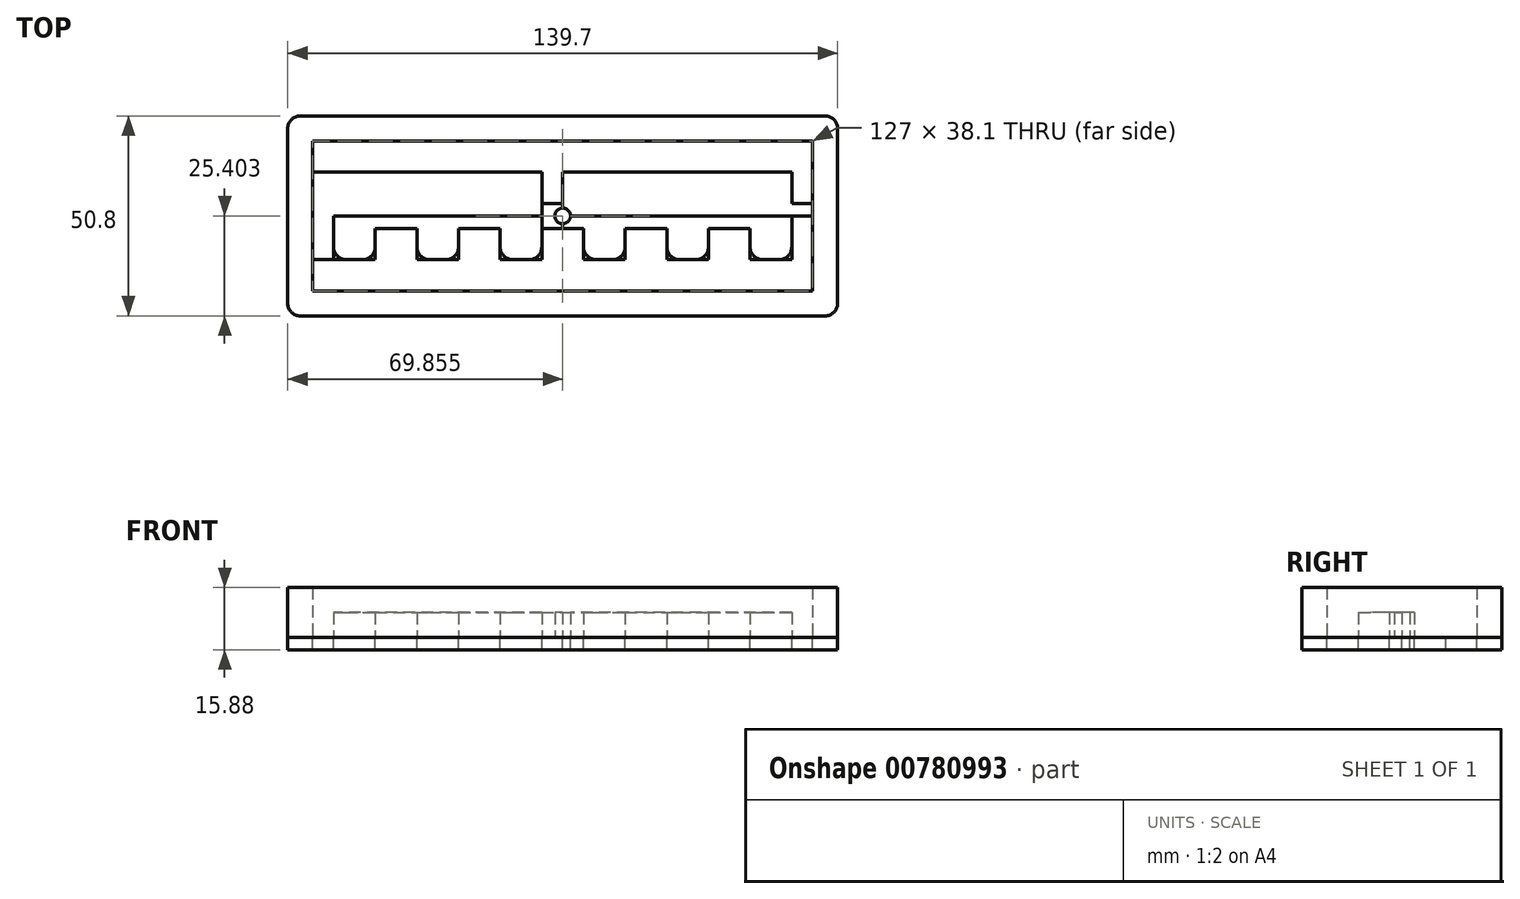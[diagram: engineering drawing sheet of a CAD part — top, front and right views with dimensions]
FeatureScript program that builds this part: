
annotation { "Feature Type Name" : "Feature", "Feature Type Description" : "" }
export const myFeature = defineFeature(function(context is Context, id is Id, definition is map)
    precondition{}
    {
        {
            var Q0;
            Q0=qCreatedBy(makeId("Top.planeOp"),FACE);
            var sketch = newSketch(context, id + "F0", { "sketchPlane" : qUnion([Q0])});
            skLineSegment(sketch, "E0.bottom", {"start": v(-62.65, 20.21) * mm, "end": v(77.05, 20.21) * mm});
            skLineSegment(sketch, "E0.top", {"start": v(-62.65, -30.59) * mm, "end": v(77.05, -30.59) * mm});
            skLineSegment(sketch, "E0.left", {"start": v(-62.65, 20.21) * mm, "end": v(-62.65, -30.59) * mm});
            skLineSegment(sketch, "E0.right", {"start": v(77.05, 20.21) * mm, "end": v(77.05, -30.59) * mm});
            skLineSegment(sketch, "E1.bottom", {"start": v(-56.3, 13.86) * mm, "end": v(70.7, 13.86) * mm});
            skLineSegment(sketch, "E1.top", {"start": v(-56.3, -24.24) * mm, "end": v(70.7, -24.24) * mm});
            skLineSegment(sketch, "E1.left", {"start": v(-56.3, 13.86) * mm, "end": v(-56.3, -24.24) * mm});
            skLineSegment(sketch, "E1.right", {"start": v(70.7, 13.86) * mm, "end": v(70.7, -24.24) * mm});
            skLineSegment(sketch, "E2", {"start": v(-56.3, 13.86) * mm, "end": v(-56.3, 20.21) * mm});
            skLineSegment(sketch, "E3", {"start": v(-56.3, 13.86) * mm, "end": v(-62.65, 13.86) * mm});
            skLineSegment(sketch, "E4", {"start": v(70.7, 13.86) * mm, "end": v(70.7, -5.19) * mm});
            skLineSegment(sketch, "E5", {"start": v(70.7, -5.19) * mm, "end": v(-56.3, -5.19) * mm});
            skLineSegment(sketch, "E6", {"start": v(-56.3, -5.19) * mm, "end": v(-56.3, -2.01) * mm});
            skLineSegment(sketch, "E7", {"start": v(-56.3, -5.19) * mm, "end": v(-56.3, -8.36) * mm});
            skLineSegment(sketch, "E8", {"start": v(-56.3, -8.36) * mm, "end": v(70.7, -8.36) * mm});
            skLineSegment(sketch, "E9", {"start": v(-56.3, -2.01) * mm, "end": v(70.7, -2.01) * mm});
            skLineSegment(sketch, "E10", {"start": v(-56.3, 13.86) * mm, "end": v(7.2, 13.86) * mm});
            skLineSegment(sketch, "E11", {"start": v(-56.3, -2.01) * mm, "end": v(-35.13, -2.01) * mm});
            skLineSegment(sketch, "E12", {"start": v(7.2, 13.86) * mm, "end": v(7.2, -2.01) * mm});
            skLineSegment(sketch, "E13", {"start": v(-35.13, -2.01) * mm, "end": v(-13.96, -2.01) * mm});
            skLineSegment(sketch, "E14", {"start": v(7.2, -2.01) * mm, "end": v(28.37, -2.01) * mm});
            skLineSegment(sketch, "E15", {"start": v(28.37, -2.01) * mm, "end": v(49.54, -2.01) * mm});
            skLineSegment(sketch, "E16", {"start": v(-35.13, -2.01) * mm, "end": v(-45.71, -2.01) * mm});
            skLineSegment(sketch, "E17", {"start": v(-35.13, -2.01) * mm, "end": v(-24.55, -2.01) * mm});
            skLineSegment(sketch, "E18", {"start": v(-13.96, -2.01) * mm, "end": v(-3.38, -2.01) * mm});
            skLineSegment(sketch, "E19", {"start": v(7.2, -2.01) * mm, "end": v(17.79, -2.01) * mm});
            skLineSegment(sketch, "E20", {"start": v(49.54, -2.01) * mm, "end": v(60.12, -2.01) * mm});
            skLineSegment(sketch, "E21", {"start": v(28.37, -2.01) * mm, "end": v(38.95, -2.01) * mm});
            skLineSegment(sketch, "E22", {"start": v(-35.13, -2.01) * mm, "end": v(-40.42, -2.01) * mm});
            skLineSegment(sketch, "E23", {"start": v(-56.3, -2.01) * mm, "end": v(-51, -2.01) * mm});
            skLineSegment(sketch, "E24", {"start": v(-51, -2.01) * mm, "end": v(-51, -8.36) * mm});
            skLineSegment(sketch, "E25", {"start": v(-40.42, -2.01) * mm, "end": v(-40.42, -8.36) * mm});
            skLineSegment(sketch, "E26", {"start": v(-35.13, -2.01) * mm, "end": v(-29.84, -2.01) * mm});
            skLineSegment(sketch, "E27", {"start": v(-13.96, -2.01) * mm, "end": v(-19.25, -2.01) * mm});
            skLineSegment(sketch, "E28", {"start": v(-29.84, -2.01) * mm, "end": v(-29.84, -8.36) * mm});
            skLineSegment(sketch, "E29", {"start": v(-19.25, -2.01) * mm, "end": v(-19.25, -8.36) * mm});
            skLineSegment(sketch, "E30", {"start": v(-13.96, -2.01) * mm, "end": v(-8.67, -2.01) * mm});
            skLineSegment(sketch, "E31", {"start": v(-8.67, -2.01) * mm, "end": v(-8.67, -8.36) * mm});
            skLineSegment(sketch, "E32", {"start": v(-3.38, -2.01) * mm, "end": v(1.91, -2.01) * mm});
            skLineSegment(sketch, "E33", {"start": v(1.91, -2.01) * mm, "end": v(1.91, -8.36) * mm});
            skLineSegment(sketch, "E34", {"start": v(7.2, -2.01) * mm, "end": v(12.5, -2.01) * mm});
            skLineSegment(sketch, "E35", {"start": v(12.5, -2.01) * mm, "end": v(12.5, -8.36) * mm});
            skLineSegment(sketch, "E36", {"start": v(17.79, -2.01) * mm, "end": v(23.08, -2.01) * mm});
            skLineSegment(sketch, "E37", {"start": v(23.08, -2.01) * mm, "end": v(23.08, -8.36) * mm});
            skLineSegment(sketch, "E38", {"start": v(28.37, -2.01) * mm, "end": v(33.66, -2.01) * mm});
            skLineSegment(sketch, "E39", {"start": v(33.66, -2.01) * mm, "end": v(33.66, -8.36) * mm});
            skLineSegment(sketch, "E40", {"start": v(38.95, -2.01) * mm, "end": v(44.25, -2.01) * mm});
            skLineSegment(sketch, "E41", {"start": v(44.25, -2.01) * mm, "end": v(44.25, -8.36) * mm});
            skLineSegment(sketch, "E42", {"start": v(49.54, -2.01) * mm, "end": v(54.83, -2.01) * mm});
            skLineSegment(sketch, "E43", {"start": v(54.83, -2.01) * mm, "end": v(54.83, -8.36) * mm});
            skLineSegment(sketch, "E44", {"start": v(60.12, -2.01) * mm, "end": v(65.41, -2.01) * mm});
            skLineSegment(sketch, "E45", {"start": v(65.41, -2.01) * mm, "end": v(65.41, -8.36) * mm});
            skLineSegment(sketch, "E46", {"start": v(-56.3, -2.01) * mm, "end": v(-56.3, 5.93) * mm});
            skLineSegment(sketch, "E47", {"start": v(-56.3, 5.93) * mm, "end": v(70.7, 5.93) * mm});
            skLineSegment(sketch, "E48", {"start": v(-51, -2.01) * mm, "end": v(-51, 5.93) * mm});
            skLineSegment(sketch, "E49", {"start": v(-40.42, -2.01) * mm, "end": v(-40.42, 5.93) * mm});
            skLineSegment(sketch, "E50", {"start": v(-29.84, -2.01) * mm, "end": v(-29.84, 5.93) * mm});
            skLineSegment(sketch, "E51", {"start": v(-19.25, -2.01) * mm, "end": v(-19.25, 5.93) * mm});
            skLineSegment(sketch, "E52", {"start": v(-8.67, -2.01) * mm, "end": v(-8.67, 5.93) * mm});
            skLineSegment(sketch, "E53", {"start": v(1.91, -2.01) * mm, "end": v(1.91, 5.93) * mm});
            skPoint(sketch, "E53.endSnap0", {"position": v(7.2, 5.93) * mm});
            skLineSegment(sketch, "E54", {"start": v(12.5, -2.01) * mm, "end": v(12.5, 5.93) * mm});
            skLineSegment(sketch, "E55", {"start": v(23.08, 5.93) * mm, "end": v(23.08, -2.01) * mm});
            skLineSegment(sketch, "E56", {"start": v(33.66, -2.01) * mm, "end": v(33.66, 5.93) * mm});
            skLineSegment(sketch, "E57", {"start": v(44.25, -2.01) * mm, "end": v(44.25, 5.93) * mm});
            skLineSegment(sketch, "E58", {"start": v(54.83, -2.01) * mm, "end": v(54.83, 5.93) * mm});
            skLineSegment(sketch, "E59", {"start": v(65.41, -2.01) * mm, "end": v(65.41, 5.93) * mm});
            skLineSegment(sketch, "E60", {"start": v(-56.3, -8.36) * mm, "end": v(-56.3, -16.3) * mm});
            skLineSegment(sketch, "E61", {"start": v(-56.3, -16.3) * mm, "end": v(70.7, -16.3) * mm});
            skLineSegment(sketch, "E62", {"start": v(-51, -8.36) * mm, "end": v(-51, -16.3) * mm});
            skLineSegment(sketch, "E63", {"start": v(-40.42, -8.36) * mm, "end": v(-40.42, -16.3) * mm});
            skLineSegment(sketch, "E64", {"start": v(-29.84, -8.36) * mm, "end": v(-29.84, -16.3) * mm});
            skLineSegment(sketch, "E65", {"start": v(-19.25, -8.36) * mm, "end": v(-19.25, -16.3) * mm});
            skLineSegment(sketch, "E66", {"start": v(-8.67, -8.36) * mm, "end": v(-8.67, -16.3) * mm});
            skLineSegment(sketch, "E67", {"start": v(1.91, -8.36) * mm, "end": v(1.91, -16.3) * mm});
            skLineSegment(sketch, "E68", {"start": v(12.5, -8.36) * mm, "end": v(12.5, -16.3) * mm});
            skLineSegment(sketch, "E69", {"start": v(23.08, -8.36) * mm, "end": v(23.08, -16.3) * mm});
            skLineSegment(sketch, "E70", {"start": v(33.66, -8.36) * mm, "end": v(33.66, -16.3) * mm});
            skLineSegment(sketch, "E71", {"start": v(44.25, -8.36) * mm, "end": v(44.25, -16.3) * mm});
            skLineSegment(sketch, "E72", {"start": v(54.83, -8.36) * mm, "end": v(54.83, -16.3) * mm});
            skLineSegment(sketch, "E73", {"start": v(65.41, -8.36) * mm, "end": v(65.41, -16.3) * mm});
            skLineSegment(sketch, "E74", {"start": v(70.7, 13.86) * mm, "end": v(77.05, 13.86) * mm});
            skLineSegment(sketch, "E75", {"start": v(-56.3, -24.24) * mm, "end": v(-62.65, -24.24) * mm});
            skLineSegment(sketch, "E76", {"start": v(70.7, -24.24) * mm, "end": v(77.05, -24.24) * mm});
            skLineSegment(sketch, "E77", {"start": v(7.2, -2.01) * mm, "end": v(7.2, -8.36) * mm});
            skCircle(sketch, "E78", {"center": v(7.2, -5.19) * mm, "radius": 2 * mm});
            skSolve(sketch);
        }
        {
            var Q0;
            {var subQ3=sQuery(id+"F0.wireOp",EDGE,"E2");Q0=makeQuery(id+"F0.imprint","IMPRINT",FACE,{"disambiguationData":[TD([[makeQuery(id+"F0.imprint","IMPRINT",EDGE,{"derivedFrom":subQ3}),1.0]])]});}
            extrude(context, id + "F1", {"entities" : qUnion([Q0]), "depth" : 12.7 * mm, "offsetDistance" : 25.4 * mm});
        }
        {
            var Q0;
            {var subQ0=sQuery(id+"F0.wireOp",EDGE,"E35");var subQ1=sQuery(id+"F0.wireOp",EDGE,"E5");var subQ2=makeQuery(id+"F0.imprint","INTERSECT",VERTEX,{"derivedFrom":[subQ1,subQ0]});Q0=makeQuery(id+"F0.imprint","IMPRINT",FACE,{"disambiguationData":[TD([[makeQuery(id+"F0.imprint","IMPRINT",EDGE,{"disambiguationData":[TD([[subQ2,-1.0]])],"derivedFrom":subQ1}),1.0]])]});}
            var Q1;
            {var subQ0=sQuery(id+"F0.wireOp",EDGE,"E33");var subQ1=sQuery(id+"F0.wireOp",EDGE,"E5");var subQ2=makeQuery(id+"F0.imprint","INTERSECT",VERTEX,{"derivedFrom":[subQ1,subQ0]});Q1=makeQuery(id+"F0.imprint","IMPRINT",FACE,{"disambiguationData":[TD([[makeQuery(id+"F0.imprint","IMPRINT",EDGE,{"disambiguationData":[TD([[subQ2,-1.0]])],"derivedFrom":subQ1}),1.0]])]});}
            var Q2;
            {var subQ0=sQuery(id+"F0.wireOp",EDGE,"E31");var subQ1=sQuery(id+"F0.wireOp",EDGE,"E5");var subQ2=makeQuery(id+"F0.imprint","INTERSECT",VERTEX,{"derivedFrom":[subQ1,subQ0]});Q2=makeQuery(id+"F0.imprint","IMPRINT",FACE,{"disambiguationData":[TD([[makeQuery(id+"F0.imprint","IMPRINT",EDGE,{"disambiguationData":[TD([[subQ2,-1.0]])],"derivedFrom":subQ1}),1.0]])]});}
            var Q3;
            {var subQ0=sQuery(id+"F0.wireOp",EDGE,"E29");var subQ1=sQuery(id+"F0.wireOp",EDGE,"E5");var subQ2=makeQuery(id+"F0.imprint","INTERSECT",VERTEX,{"derivedFrom":[subQ1,subQ0]});Q3=makeQuery(id+"F0.imprint","IMPRINT",FACE,{"disambiguationData":[TD([[makeQuery(id+"F0.imprint","IMPRINT",EDGE,{"disambiguationData":[TD([[subQ2,-1.0]])],"derivedFrom":subQ1}),1.0]])]});}
            var Q4;
            {var subQ0=sQuery(id+"F0.wireOp",EDGE,"E28");var subQ1=sQuery(id+"F0.wireOp",EDGE,"E5");var subQ2=makeQuery(id+"F0.imprint","INTERSECT",VERTEX,{"derivedFrom":[subQ1,subQ0]});Q4=makeQuery(id+"F0.imprint","IMPRINT",FACE,{"disambiguationData":[TD([[makeQuery(id+"F0.imprint","IMPRINT",EDGE,{"disambiguationData":[TD([[subQ2,-1.0]])],"derivedFrom":subQ1}),1.0]])]});}
            var Q5;
            {var subQ0=sQuery(id+"F0.wireOp",EDGE,"E25");var subQ1=sQuery(id+"F0.wireOp",EDGE,"E5");var subQ2=makeQuery(id+"F0.imprint","INTERSECT",VERTEX,{"derivedFrom":[subQ1,subQ0]});Q5=makeQuery(id+"F0.imprint","IMPRINT",FACE,{"disambiguationData":[TD([[makeQuery(id+"F0.imprint","IMPRINT",EDGE,{"disambiguationData":[TD([[subQ2,-1.0]])],"derivedFrom":subQ1}),1.0]])]});}
            var Q6;
            {var subQ1=sQuery(id+"F0.wireOp",EDGE,"E11");Q6=makeQuery(id+"F0.imprint","IMPRINT",FACE,{"disambiguationData":[TD([[makeQuery(id+"F0.imprint","IMPRINT",EDGE,{"derivedFrom":subQ1}),-1.0]])]});}
            var Q7;
            {var subQ2=sQuery(id+"F0.wireOp",EDGE,"E22");Q7=makeQuery(id+"F0.imprint","IMPRINT",FACE,{"disambiguationData":[TD([[makeQuery(id+"F0.imprint","IMPRINT",EDGE,{"derivedFrom":subQ2}),1.0]])]});}
            var Q8;
            {var subQ4=sQuery(id+"F0.wireOp",EDGE,"E13");Q8=makeQuery(id+"F0.imprint","IMPRINT",FACE,{"disambiguationData":[TD([[makeQuery(id+"F0.imprint","IMPRINT",EDGE,{"derivedFrom":subQ4}),-1.0]])]});}
            var Q9;
            {var subQ1=sQuery(id+"F0.wireOp",EDGE,"E27");Q9=makeQuery(id+"F0.imprint","IMPRINT",FACE,{"disambiguationData":[TD([[makeQuery(id+"F0.imprint","IMPRINT",EDGE,{"derivedFrom":subQ1}),1.0]])]});}
            var Q10;
            {var subQ2=sQuery(id+"F0.wireOp",EDGE,"E18");Q10=makeQuery(id+"F0.imprint","IMPRINT",FACE,{"disambiguationData":[TD([[makeQuery(id+"F0.imprint","IMPRINT",EDGE,{"derivedFrom":subQ2}),-1.0]])]});}
            var Q11;
            {var subQ5=sQuery(id+"F0.wireOp",EDGE,"E34");Q11=makeQuery(id+"F0.imprint","IMPRINT",FACE,{"disambiguationData":[TD([[makeQuery(id+"F0.imprint","IMPRINT",EDGE,{"derivedFrom":subQ5}),-1.0]])]});}
            var Q12;
            {var subQ2=sQuery(id+"F0.wireOp",EDGE,"E19");Q12=makeQuery(id+"F0.imprint","IMPRINT",FACE,{"disambiguationData":[TD([[makeQuery(id+"F0.imprint","IMPRINT",EDGE,{"derivedFrom":subQ2}),-1.0]])]});}
            var Q13;
            {var subQ0=sQuery(id+"F0.wireOp",EDGE,"E37");var subQ1=sQuery(id+"F0.wireOp",EDGE,"E5");var subQ2=makeQuery(id+"F0.imprint","INTERSECT",VERTEX,{"derivedFrom":[subQ1,subQ0]});Q13=makeQuery(id+"F0.imprint","IMPRINT",FACE,{"disambiguationData":[TD([[makeQuery(id+"F0.imprint","IMPRINT",EDGE,{"disambiguationData":[TD([[subQ2,-1.0]])],"derivedFrom":subQ1}),1.0]])]});}
            var Q14;
            {var subQ0=sQuery(id+"F0.wireOp",EDGE,"E39");var subQ1=sQuery(id+"F0.wireOp",EDGE,"E5");var subQ2=makeQuery(id+"F0.imprint","INTERSECT",VERTEX,{"derivedFrom":[subQ1,subQ0]});Q14=makeQuery(id+"F0.imprint","IMPRINT",FACE,{"disambiguationData":[TD([[makeQuery(id+"F0.imprint","IMPRINT",EDGE,{"disambiguationData":[TD([[subQ2,-1.0]])],"derivedFrom":subQ1}),1.0]])]});}
            var Q15;
            {var subQ2=sQuery(id+"F0.wireOp",EDGE,"E14");Q15=makeQuery(id+"F0.imprint","IMPRINT",FACE,{"disambiguationData":[TD([[makeQuery(id+"F0.imprint","IMPRINT",EDGE,{"derivedFrom":subQ2}),-1.0]])]});}
            var Q16;
            {var subQ1=sQuery(id+"F0.wireOp",EDGE,"E21");Q16=makeQuery(id+"F0.imprint","IMPRINT",FACE,{"disambiguationData":[TD([[makeQuery(id+"F0.imprint","IMPRINT",EDGE,{"derivedFrom":subQ1}),-1.0]])]});}
            var Q17;
            {var subQ0=sQuery(id+"F0.wireOp",EDGE,"E41");var subQ1=sQuery(id+"F0.wireOp",EDGE,"E5");var subQ2=makeQuery(id+"F0.imprint","INTERSECT",VERTEX,{"derivedFrom":[subQ1,subQ0]});Q17=makeQuery(id+"F0.imprint","IMPRINT",FACE,{"disambiguationData":[TD([[makeQuery(id+"F0.imprint","IMPRINT",EDGE,{"disambiguationData":[TD([[subQ2,-1.0]])],"derivedFrom":subQ1}),1.0]])]});}
            var Q18;
            {var subQ0=sQuery(id+"F0.wireOp",EDGE,"E43");var subQ1=sQuery(id+"F0.wireOp",EDGE,"E5");var subQ2=makeQuery(id+"F0.imprint","INTERSECT",VERTEX,{"derivedFrom":[subQ1,subQ0]});Q18=makeQuery(id+"F0.imprint","IMPRINT",FACE,{"disambiguationData":[TD([[makeQuery(id+"F0.imprint","IMPRINT",EDGE,{"disambiguationData":[TD([[subQ2,-1.0]])],"derivedFrom":subQ1}),1.0]])]});}
            var Q19;
            {var subQ2=sQuery(id+"F0.wireOp",EDGE,"E15");Q19=makeQuery(id+"F0.imprint","IMPRINT",FACE,{"disambiguationData":[TD([[makeQuery(id+"F0.imprint","IMPRINT",EDGE,{"derivedFrom":subQ2}),-1.0]])]});}
            var Q20;
            {var subQ1=sQuery(id+"F0.wireOp",EDGE,"E20");Q20=makeQuery(id+"F0.imprint","IMPRINT",FACE,{"disambiguationData":[TD([[makeQuery(id+"F0.imprint","IMPRINT",EDGE,{"derivedFrom":subQ1}),-1.0]])]});}
            var Q21;
            {var subQ0=sQuery(id+"F0.wireOp",EDGE,"E45");var subQ1=sQuery(id+"F0.wireOp",EDGE,"E5");var subQ2=makeQuery(id+"F0.imprint","INTERSECT",VERTEX,{"derivedFrom":[subQ1,subQ0]});Q21=makeQuery(id+"F0.imprint","IMPRINT",FACE,{"disambiguationData":[TD([[makeQuery(id+"F0.imprint","IMPRINT",EDGE,{"disambiguationData":[TD([[subQ2,-1.0]])],"derivedFrom":subQ1}),1.0]])]});}
            var Q22;
            Q22=makeQuery(id+"F0.imprint","IMPRINT",FACE,{"disambiguationData":[TD([[makeQuery(id+"F0.imprint","IMPRINT",EDGE,{"derivedFrom":sQuery(id+"F0.wireOp",EDGE,"E20")}),1.0]])]});
            var Q23;
            {var subQ0=sQuery(id+"F0.wireOp",EDGE,"E72");Q23=makeQuery(id+"F0.imprint","IMPRINT",FACE,{"disambiguationData":[TD([[makeQuery(id+"F0.imprint","IMPRINT",EDGE,{"derivedFrom":subQ0}),1.0]])]});}
            var Q24;
            {var subQ0=sQuery(id+"F0.wireOp",EDGE,"E70");Q24=makeQuery(id+"F0.imprint","IMPRINT",FACE,{"disambiguationData":[TD([[makeQuery(id+"F0.imprint","IMPRINT",EDGE,{"derivedFrom":subQ0}),1.0]])]});}
            var Q25;
            Q25=makeQuery(id+"F0.imprint","IMPRINT",FACE,{"disambiguationData":[TD([[makeQuery(id+"F0.imprint","IMPRINT",EDGE,{"derivedFrom":sQuery(id+"F0.wireOp",EDGE,"E21")}),1.0]])]});
            var Q26;
            Q26=makeQuery(id+"F0.imprint","IMPRINT",FACE,{"disambiguationData":[TD([[makeQuery(id+"F0.imprint","IMPRINT",EDGE,{"derivedFrom":sQuery(id+"F0.wireOp",EDGE,"E19")}),1.0]])]});
            var Q27;
            {var subQ0=sQuery(id+"F0.wireOp",EDGE,"E68");Q27=makeQuery(id+"F0.imprint","IMPRINT",FACE,{"disambiguationData":[TD([[makeQuery(id+"F0.imprint","IMPRINT",EDGE,{"derivedFrom":subQ0}),1.0]])]});}
            var Q28;
            {var subQ0=sQuery(id+"F0.wireOp",EDGE,"E66");Q28=makeQuery(id+"F0.imprint","IMPRINT",FACE,{"disambiguationData":[TD([[makeQuery(id+"F0.imprint","IMPRINT",EDGE,{"derivedFrom":subQ0}),1.0]])]});}
            var Q29;
            Q29=makeQuery(id+"F0.imprint","IMPRINT",FACE,{"disambiguationData":[TD([[makeQuery(id+"F0.imprint","IMPRINT",EDGE,{"derivedFrom":sQuery(id+"F0.wireOp",EDGE,"E18")}),1.0]])]});
            var Q30;
            Q30=makeQuery(id+"F0.imprint","IMPRINT",FACE,{"disambiguationData":[TD([[makeQuery(id+"F0.imprint","IMPRINT",EDGE,{"derivedFrom":sQuery(id+"F0.wireOp",EDGE,"E13")}),1.0]])]});
            var Q31;
            {var subQ0=sQuery(id+"F0.wireOp",EDGE,"E64");Q31=makeQuery(id+"F0.imprint","IMPRINT",FACE,{"disambiguationData":[TD([[makeQuery(id+"F0.imprint","IMPRINT",EDGE,{"derivedFrom":subQ0}),1.0]])]});}
            var Q32;
            {var subQ0=sQuery(id+"F0.wireOp",EDGE,"E62");Q32=makeQuery(id+"F0.imprint","IMPRINT",FACE,{"disambiguationData":[TD([[makeQuery(id+"F0.imprint","IMPRINT",EDGE,{"derivedFrom":subQ0}),1.0]])]});}
            var Q33;
            Q33=makeQuery(id+"F0.imprint","IMPRINT",FACE,{"disambiguationData":[TD([[makeQuery(id+"F0.imprint","IMPRINT",EDGE,{"derivedFrom":sQuery(id+"F0.wireOp",EDGE,"E11")}),1.0]])]});
            extrude(context, id + "F2", {"entities" : qUnion([Q0, Q1, Q2, Q3, Q4, Q5, Q6, Q7, Q8, Q9, Q10, Q11, Q12, Q13, Q14, Q15, Q16, Q17, Q18, Q19, Q20, Q21, Q22, Q23, Q24, Q25, Q26, Q27, Q28, Q29, Q30, Q31, Q32, Q33]), "depth" : 6.35 * mm, "offsetDistance" : 25.4 * mm});
        }
        {
            var Q0;
            Q0=makeQuery(id+"F0.imprint","IMPRINT",FACE,{"disambiguationData":[TD([[makeQuery(id+"F0.imprint","IMPRINT",EDGE,{"derivedFrom":sQuery(id+"F0.wireOp",EDGE,"E1.bottom")}),1.0]])]});
            extrude(context, id + "F3", {"entities" : qUnion([Q0]), "operationType" : NewBodyOperationType.ADD, "depth" : 12.7 * mm, "offsetDistance" : 25.4 * mm});
        }
        {
            var Q0;
            {var subQ0=sQuery(id+"F0.wireOp",EDGE,"E3");Q0=makeQuery(id+"F0.imprint","IMPRINT",FACE,{"disambiguationData":[TD([[makeQuery(id+"F0.imprint","IMPRINT",EDGE,{"derivedFrom":subQ0}),1.0]])]});}
            var Q1;
            {var subQ1=sQuery(id+"F0.wireOp",EDGE,"E0.top");Q1=makeQuery(id+"F0.imprint","IMPRINT",FACE,{"disambiguationData":[TD([[makeQuery(id+"F0.imprint","IMPRINT",EDGE,{"derivedFrom":subQ1}),1.0]])]});}
            var Q2;
            {var subQ6=sQuery(id+"F0.wireOp",EDGE,"E74");Q2=makeQuery(id+"F0.imprint","IMPRINT",FACE,{"disambiguationData":[TD([[makeQuery(id+"F0.imprint","IMPRINT",EDGE,{"derivedFrom":subQ6}),-1.0]])]});}
            extrude(context, id + "F4", {"entities" : qUnion([Q0, Q1, Q2]), "operationType" : NewBodyOperationType.ADD, "depth" : 12.7 * mm, "offsetDistance" : 25.4 * mm});
        }
        {
            var Q0;
            {var subQ3=sQuery(id+"F0.wireOp",EDGE,"E78");var subQ7=sQuery(id+"F0.wireOp",EDGE,"E5");var subQ9=makeQuery(id+"F0.imprint","INTERSECT",VERTEX,{"disambiguationData":[OD(1.0)],"derivedFrom":[subQ7,subQ3]});Q0=makeQuery(id+"F0.imprint","IMPRINT",FACE,{"disambiguationData":[TD([[makeQuery(id+"F0.imprint","IMPRINT",EDGE,{"disambiguationData":[TD([[subQ9,-1.0]])],"derivedFrom":subQ7}),1.0]])]});}
            var Q1;
            {var subQ3=sQuery(id+"F0.wireOp",EDGE,"E5");var subQ7=sQuery(id+"F0.wireOp",EDGE,"E78");var subQ9=makeQuery(id+"F0.imprint","INTERSECT",VERTEX,{"disambiguationData":[OD(1.0)],"derivedFrom":[subQ3,subQ7]});Q1=makeQuery(id+"F0.imprint","IMPRINT",FACE,{"disambiguationData":[TD([[makeQuery(id+"F0.imprint","IMPRINT",EDGE,{"disambiguationData":[TD([[subQ9,-1.0]])],"derivedFrom":subQ3}),-1.0]])]});}
            extrude(context, id + "F5", {"entities" : qUnion([Q0, Q1]), "depth" : 6.35 * mm, "offsetDistance" : 25.4 * mm});
        }
        {
            var Q0;
            {var subQ7=sQuery(id+"F0.wireOp",EDGE,"E1.top");Q0=makeQuery(id+"F0.imprint","IMPRINT",FACE,{"disambiguationData":[TD([[makeQuery(id+"F0.imprint","IMPRINT",EDGE,{"derivedFrom":subQ7}),1.0]])]});}
            var Q1;
            {var subQ0=sQuery(id+"F0.wireOp",EDGE,"E60");Q1=makeQuery(id+"F0.imprint","IMPRINT",FACE,{"disambiguationData":[TD([[makeQuery(id+"F0.imprint","IMPRINT",EDGE,{"derivedFrom":subQ0}),1.0]])]});}
            var Q2;
            {var subQ0=sQuery(id+"F0.wireOp",EDGE,"E6");Q2=makeQuery(id+"F0.imprint","IMPRINT",FACE,{"disambiguationData":[TD([[makeQuery(id+"F0.imprint","IMPRINT",EDGE,{"derivedFrom":subQ0}),-1.0]])]});}
            var Q3;
            {var subQ0=sQuery(id+"F0.wireOp",EDGE,"E7");Q3=makeQuery(id+"F0.imprint","IMPRINT",FACE,{"disambiguationData":[TD([[makeQuery(id+"F0.imprint","IMPRINT",EDGE,{"derivedFrom":subQ0}),1.0]])]});}
            var Q4;
            Q4=makeQuery(id+"F0.imprint","IMPRINT",FACE,{"disambiguationData":[TD([[makeQuery(id+"F0.imprint","IMPRINT",EDGE,{"derivedFrom":sQuery(id+"F0.wireOp",EDGE,"E23")}),1.0]])]});
            var Q5;
            {var subQ1=sQuery(id+"F0.wireOp",EDGE,"E10");Q5=makeQuery(id+"F0.imprint","IMPRINT",FACE,{"disambiguationData":[TD([[makeQuery(id+"F0.imprint","IMPRINT",EDGE,{"derivedFrom":subQ1}),-1.0]])]});}
            var Q6;
            {var subQ4=sQuery(id+"F0.wireOp",EDGE,"E1.bottom");Q6=makeQuery(id+"F0.imprint","IMPRINT",FACE,{"disambiguationData":[TD([[makeQuery(id+"F0.imprint","IMPRINT",EDGE,{"derivedFrom":subQ4}),-1.0]])]});}
            var Q7;
            {var subQ5=sQuery(id+"F0.wireOp",EDGE,"E59");Q7=makeQuery(id+"F0.imprint","IMPRINT",FACE,{"disambiguationData":[TD([[makeQuery(id+"F0.imprint","IMPRINT",EDGE,{"derivedFrom":subQ5}),-1.0]])]});}
            var Q8;
            {var subQ1=sQuery(id+"F0.wireOp",EDGE,"E4");var subQ3=sQuery(id+"F0.wireOp",EDGE,"E9");var subQ4=makeQuery(id+"F0.imprint","INTERSECT",VERTEX,{"derivedFrom":[subQ1,subQ3]});Q8=makeQuery(id+"F0.imprint","IMPRINT",FACE,{"disambiguationData":[TD([[makeQuery(id+"F0.imprint","IMPRINT",EDGE,{"disambiguationData":[TD([[subQ4,-1.0]])],"derivedFrom":subQ1}),-1.0]])]});}
            var Q9;
            {var subQ1=sQuery(id+"F0.wireOp",EDGE,"E1.right");var subQ3=sQuery(id+"F0.wireOp",EDGE,"E8");var subQ4=makeQuery(id+"F0.imprint","INTERSECT",VERTEX,{"derivedFrom":[subQ1,subQ3]});Q9=makeQuery(id+"F0.imprint","IMPRINT",FACE,{"disambiguationData":[TD([[makeQuery(id+"F0.imprint","IMPRINT",EDGE,{"disambiguationData":[TD([[subQ4,1.0]])],"derivedFrom":subQ1}),-1.0]])]});}
            var Q10;
            {var subQ5=sQuery(id+"F0.wireOp",EDGE,"E73");Q10=makeQuery(id+"F0.imprint","IMPRINT",FACE,{"disambiguationData":[TD([[makeQuery(id+"F0.imprint","IMPRINT",EDGE,{"derivedFrom":subQ5}),1.0]])]});}
            var Q11;
            {var subQ0=sQuery(id+"F0.wireOp",EDGE,"E71");Q11=makeQuery(id+"F0.imprint","IMPRINT",FACE,{"disambiguationData":[TD([[makeQuery(id+"F0.imprint","IMPRINT",EDGE,{"derivedFrom":subQ0}),1.0]])]});}
            var Q12;
            Q12=makeQuery(id+"F0.imprint","IMPRINT",FACE,{"disambiguationData":[TD([[makeQuery(id+"F0.imprint","IMPRINT",EDGE,{"derivedFrom":sQuery(id+"F0.wireOp",EDGE,"E15")}),1.0]])]});
            var Q13;
            Q13=makeQuery(id+"F0.imprint","IMPRINT",FACE,{"disambiguationData":[TD([[makeQuery(id+"F0.imprint","IMPRINT",EDGE,{"derivedFrom":sQuery(id+"F0.wireOp",EDGE,"E14")}),1.0]])]});
            var Q14;
            {var subQ0=sQuery(id+"F0.wireOp",EDGE,"E53");Q14=makeQuery(id+"F0.imprint","IMPRINT",FACE,{"disambiguationData":[TD([[makeQuery(id+"F0.imprint","IMPRINT",EDGE,{"derivedFrom":subQ0}),-1.0]])]});}
            var Q15;
            {var subQ0=sQuery(id+"F0.wireOp",EDGE,"E34");Q15=makeQuery(id+"F0.imprint","IMPRINT",FACE,{"disambiguationData":[TD([[makeQuery(id+"F0.imprint","IMPRINT",EDGE,{"derivedFrom":subQ0}),1.0]])]});}
            var Q16;
            Q16=makeQuery(id+"F0.imprint","IMPRINT",FACE,{"disambiguationData":[TD([[makeQuery(id+"F0.imprint","IMPRINT",EDGE,{"derivedFrom":sQuery(id+"F0.wireOp",EDGE,"E27")}),-1.0]])]});
            var Q17;
            Q17=makeQuery(id+"F0.imprint","IMPRINT",FACE,{"disambiguationData":[TD([[makeQuery(id+"F0.imprint","IMPRINT",EDGE,{"derivedFrom":sQuery(id+"F0.wireOp",EDGE,"E22")}),-1.0]])]});
            var Q18;
            {var subQ0=sQuery(id+"F0.wireOp",EDGE,"E65");Q18=makeQuery(id+"F0.imprint","IMPRINT",FACE,{"disambiguationData":[TD([[makeQuery(id+"F0.imprint","IMPRINT",EDGE,{"derivedFrom":subQ0}),1.0]])]});}
            var Q19;
            {var subQ0=sQuery(id+"F0.wireOp",EDGE,"E67");Q19=makeQuery(id+"F0.imprint","IMPRINT",FACE,{"disambiguationData":[TD([[makeQuery(id+"F0.imprint","IMPRINT",EDGE,{"derivedFrom":subQ0}),1.0]])]});}
            var Q20;
            {var subQ0=sQuery(id+"F0.wireOp",EDGE,"E69");Q20=makeQuery(id+"F0.imprint","IMPRINT",FACE,{"disambiguationData":[TD([[makeQuery(id+"F0.imprint","IMPRINT",EDGE,{"derivedFrom":subQ0}),1.0]])]});}
            var Q21;
            {var subQ0=sQuery(id+"F0.wireOp",EDGE,"E63");Q21=makeQuery(id+"F0.imprint","IMPRINT",FACE,{"disambiguationData":[TD([[makeQuery(id+"F0.imprint","IMPRINT",EDGE,{"derivedFrom":subQ0}),1.0]])]});}
            extrude(context, id + "F6", {"entities" : qUnion([Q0, Q1, Q2, Q3, Q4, Q5, Q6, Q7, Q8, Q9, Q10, Q11, Q12, Q13, Q14, Q15, Q16, Q17, Q18, Q19, Q20, Q21]), "oppositeDirection" : true, "depth" : 3.17 * mm, "offsetDistance" : 25.4 * mm});
        }
        {
            var Q0;
            {var subQ1=sQuery(id+"F0.wireOp",EDGE,"E0.top");Q0=makeQuery(id+"F0.imprint","IMPRINT",FACE,{"disambiguationData":[TD([[makeQuery(id+"F0.imprint","IMPRINT",EDGE,{"derivedFrom":subQ1}),1.0]])]});}
            var Q1;
            {var subQ0=sQuery(id+"F0.wireOp",EDGE,"E3");Q1=makeQuery(id+"F0.imprint","IMPRINT",FACE,{"disambiguationData":[TD([[makeQuery(id+"F0.imprint","IMPRINT",EDGE,{"derivedFrom":subQ0}),1.0]])]});}
            var Q2;
            {var subQ3=sQuery(id+"F0.wireOp",EDGE,"E2");Q2=makeQuery(id+"F0.imprint","IMPRINT",FACE,{"disambiguationData":[TD([[makeQuery(id+"F0.imprint","IMPRINT",EDGE,{"derivedFrom":subQ3}),1.0]])]});}
            var Q3;
            Q3=makeQuery(id+"F0.imprint","IMPRINT",FACE,{"disambiguationData":[TD([[makeQuery(id+"F0.imprint","IMPRINT",EDGE,{"derivedFrom":sQuery(id+"F0.wireOp",EDGE,"E1.bottom")}),1.0]])]});
            var Q4;
            {var subQ4=sQuery(id+"F0.wireOp",EDGE,"E74");Q4=makeQuery(id+"F0.imprint","IMPRINT",FACE,{"disambiguationData":[TD([[makeQuery(id+"F0.imprint","IMPRINT",EDGE,{"derivedFrom":subQ4}),-1.0]])]});}
            extrude(context, id + "F7", {"entities" : qUnion([Q0, Q1, Q2, Q3, Q4]), "oppositeDirection" : true, "depth" : 3.17 * mm, "offsetDistance" : 25.4 * mm});
        }
        {
            var Q0;
            Q0=makeQuery(id+"F0.imprint","IMPRINT",FACE,{"disambiguationData":[TD([[makeQuery(id+"F0.imprint","IMPRINT",EDGE,{"derivedFrom":sQuery(id+"F0.wireOp",EDGE,"E11")}),1.0]])]});
            var Q1;
            {var subQ1=sQuery(id+"F0.wireOp",EDGE,"E11");Q1=makeQuery(id+"F0.imprint","IMPRINT",FACE,{"disambiguationData":[TD([[makeQuery(id+"F0.imprint","IMPRINT",EDGE,{"derivedFrom":subQ1}),-1.0]])]});}
            var Q2;
            {var subQ0=sQuery(id+"F0.wireOp",EDGE,"E25");var subQ1=sQuery(id+"F0.wireOp",EDGE,"E5");var subQ2=makeQuery(id+"F0.imprint","INTERSECT",VERTEX,{"derivedFrom":[subQ1,subQ0]});Q2=makeQuery(id+"F0.imprint","IMPRINT",FACE,{"disambiguationData":[TD([[makeQuery(id+"F0.imprint","IMPRINT",EDGE,{"disambiguationData":[TD([[subQ2,-1.0]])],"derivedFrom":subQ1}),1.0]])]});}
            var Q3;
            {var subQ0=sQuery(id+"F0.wireOp",EDGE,"E62");Q3=makeQuery(id+"F0.imprint","IMPRINT",FACE,{"disambiguationData":[TD([[makeQuery(id+"F0.imprint","IMPRINT",EDGE,{"derivedFrom":subQ0}),1.0]])]});}
            var Q4;
            {var subQ0=sQuery(id+"F0.wireOp",EDGE,"E28");var subQ1=sQuery(id+"F0.wireOp",EDGE,"E5");var subQ2=makeQuery(id+"F0.imprint","INTERSECT",VERTEX,{"derivedFrom":[subQ1,subQ0]});Q4=makeQuery(id+"F0.imprint","IMPRINT",FACE,{"disambiguationData":[TD([[makeQuery(id+"F0.imprint","IMPRINT",EDGE,{"disambiguationData":[TD([[subQ2,-1.0]])],"derivedFrom":subQ1}),1.0]])]});}
            var Q5;
            {var subQ1=sQuery(id+"F0.wireOp",EDGE,"E22");Q5=makeQuery(id+"F0.imprint","IMPRINT",FACE,{"disambiguationData":[TD([[makeQuery(id+"F0.imprint","IMPRINT",EDGE,{"derivedFrom":subQ1}),1.0]])]});}
            var Q6;
            Q6=makeQuery(id+"F0.imprint","IMPRINT",FACE,{"disambiguationData":[TD([[makeQuery(id+"F0.imprint","IMPRINT",EDGE,{"derivedFrom":sQuery(id+"F0.wireOp",EDGE,"E13")}),1.0]])]});
            var Q7;
            {var subQ4=sQuery(id+"F0.wireOp",EDGE,"E13");Q7=makeQuery(id+"F0.imprint","IMPRINT",FACE,{"disambiguationData":[TD([[makeQuery(id+"F0.imprint","IMPRINT",EDGE,{"derivedFrom":subQ4}),-1.0]])]});}
            var Q8;
            {var subQ0=sQuery(id+"F0.wireOp",EDGE,"E29");var subQ1=sQuery(id+"F0.wireOp",EDGE,"E5");var subQ2=makeQuery(id+"F0.imprint","INTERSECT",VERTEX,{"derivedFrom":[subQ1,subQ0]});Q8=makeQuery(id+"F0.imprint","IMPRINT",FACE,{"disambiguationData":[TD([[makeQuery(id+"F0.imprint","IMPRINT",EDGE,{"disambiguationData":[TD([[subQ2,-1.0]])],"derivedFrom":subQ1}),1.0]])]});}
            var Q9;
            {var subQ0=sQuery(id+"F0.wireOp",EDGE,"E64");Q9=makeQuery(id+"F0.imprint","IMPRINT",FACE,{"disambiguationData":[TD([[makeQuery(id+"F0.imprint","IMPRINT",EDGE,{"derivedFrom":subQ0}),1.0]])]});}
            var Q10;
            {var subQ0=sQuery(id+"F0.wireOp",EDGE,"E31");var subQ1=sQuery(id+"F0.wireOp",EDGE,"E5");var subQ2=makeQuery(id+"F0.imprint","INTERSECT",VERTEX,{"derivedFrom":[subQ1,subQ0]});Q10=makeQuery(id+"F0.imprint","IMPRINT",FACE,{"disambiguationData":[TD([[makeQuery(id+"F0.imprint","IMPRINT",EDGE,{"disambiguationData":[TD([[subQ2,-1.0]])],"derivedFrom":subQ1}),1.0]])]});}
            var Q11;
            {var subQ1=sQuery(id+"F0.wireOp",EDGE,"E27");Q11=makeQuery(id+"F0.imprint","IMPRINT",FACE,{"disambiguationData":[TD([[makeQuery(id+"F0.imprint","IMPRINT",EDGE,{"derivedFrom":subQ1}),1.0]])]});}
            var Q12;
            {var subQ0=sQuery(id+"F0.wireOp",EDGE,"E66");Q12=makeQuery(id+"F0.imprint","IMPRINT",FACE,{"disambiguationData":[TD([[makeQuery(id+"F0.imprint","IMPRINT",EDGE,{"derivedFrom":subQ0}),1.0]])]});}
            var Q13;
            {var subQ0=sQuery(id+"F0.wireOp",EDGE,"E33");var subQ1=sQuery(id+"F0.wireOp",EDGE,"E5");var subQ2=makeQuery(id+"F0.imprint","INTERSECT",VERTEX,{"derivedFrom":[subQ1,subQ0]});Q13=makeQuery(id+"F0.imprint","IMPRINT",FACE,{"disambiguationData":[TD([[makeQuery(id+"F0.imprint","IMPRINT",EDGE,{"disambiguationData":[TD([[subQ2,-1.0]])],"derivedFrom":subQ1}),1.0]])]});}
            var Q14;
            {var subQ1=sQuery(id+"F0.wireOp",EDGE,"E18");Q14=makeQuery(id+"F0.imprint","IMPRINT",FACE,{"disambiguationData":[TD([[makeQuery(id+"F0.imprint","IMPRINT",EDGE,{"derivedFrom":subQ1}),-1.0]])]});}
            var Q15;
            Q15=makeQuery(id+"F0.imprint","IMPRINT",FACE,{"disambiguationData":[TD([[makeQuery(id+"F0.imprint","IMPRINT",EDGE,{"derivedFrom":sQuery(id+"F0.wireOp",EDGE,"E18")}),1.0]])]});
            var Q16;
            {var subQ3=sQuery(id+"F0.wireOp",EDGE,"E78");var subQ7=sQuery(id+"F0.wireOp",EDGE,"E5");var subQ9=makeQuery(id+"F0.imprint","INTERSECT",VERTEX,{"disambiguationData":[OD(1.0)],"derivedFrom":[subQ7,subQ3]});Q16=makeQuery(id+"F0.imprint","IMPRINT",FACE,{"disambiguationData":[TD([[makeQuery(id+"F0.imprint","IMPRINT",EDGE,{"disambiguationData":[TD([[subQ9,-1.0]])],"derivedFrom":subQ7}),1.0]])]});}
            var Q17;
            {var subQ3=sQuery(id+"F0.wireOp",EDGE,"E5");var subQ7=sQuery(id+"F0.wireOp",EDGE,"E78");var subQ9=makeQuery(id+"F0.imprint","INTERSECT",VERTEX,{"disambiguationData":[OD(1.0)],"derivedFrom":[subQ3,subQ7]});Q17=makeQuery(id+"F0.imprint","IMPRINT",FACE,{"disambiguationData":[TD([[makeQuery(id+"F0.imprint","IMPRINT",EDGE,{"disambiguationData":[TD([[subQ9,-1.0]])],"derivedFrom":subQ3}),-1.0]])]});}
            var Q18;
            {var subQ1=sQuery(id+"F0.wireOp",EDGE,"E34");Q18=makeQuery(id+"F0.imprint","IMPRINT",FACE,{"disambiguationData":[TD([[makeQuery(id+"F0.imprint","IMPRINT",EDGE,{"derivedFrom":subQ1}),-1.0]])]});}
            var Q19;
            {var subQ5=sQuery(id+"F0.wireOp",EDGE,"E35");var subQ7=sQuery(id+"F0.wireOp",EDGE,"E5");var subQ8=makeQuery(id+"F0.imprint","INTERSECT",VERTEX,{"derivedFrom":[subQ7,subQ5]});Q19=makeQuery(id+"F0.imprint","IMPRINT",FACE,{"disambiguationData":[TD([[makeQuery(id+"F0.imprint","IMPRINT",EDGE,{"disambiguationData":[TD([[subQ8,-1.0]])],"derivedFrom":subQ7}),1.0]])]});}
            var Q20;
            {var subQ0=sQuery(id+"F0.wireOp",EDGE,"E78");var subQ1=sQuery(id+"F0.wireOp",EDGE,"E5");var subQ2=makeQuery(id+"F0.imprint","INTERSECT",VERTEX,{"disambiguationData":[OD(0.0)],"derivedFrom":[subQ1,subQ0]});Q20=makeQuery(id+"F0.imprint","IMPRINT",FACE,{"disambiguationData":[TD([[makeQuery(id+"F0.imprint","IMPRINT",EDGE,{"disambiguationData":[TD([[subQ2,-1.0]])],"derivedFrom":subQ1}),-1.0]])]});}
            var Q21;
            {var subQ0=sQuery(id+"F0.wireOp",EDGE,"E77");var subQ1=sQuery(id+"F0.wireOp",EDGE,"E5");var subQ2=makeQuery(id+"F0.imprint","INTERSECT",VERTEX,{"derivedFrom":[subQ1,subQ0]});Q21=makeQuery(id+"F0.imprint","IMPRINT",FACE,{"disambiguationData":[TD([[makeQuery(id+"F0.imprint","IMPRINT",EDGE,{"disambiguationData":[TD([[subQ2,-1.0]])],"derivedFrom":subQ1}),-1.0]])]});}
            var Q22;
            {var subQ0=sQuery(id+"F0.wireOp",EDGE,"E77");var subQ1=sQuery(id+"F0.wireOp",EDGE,"E5");var subQ2=makeQuery(id+"F0.imprint","INTERSECT",VERTEX,{"derivedFrom":[subQ1,subQ0]});Q22=makeQuery(id+"F0.imprint","IMPRINT",FACE,{"disambiguationData":[TD([[makeQuery(id+"F0.imprint","IMPRINT",EDGE,{"disambiguationData":[TD([[subQ2,-1.0]])],"derivedFrom":subQ1}),1.0]])]});}
            var Q23;
            {var subQ0=sQuery(id+"F0.wireOp",EDGE,"E78");var subQ1=sQuery(id+"F0.wireOp",EDGE,"E5");var subQ2=makeQuery(id+"F0.imprint","INTERSECT",VERTEX,{"disambiguationData":[OD(0.0)],"derivedFrom":[subQ1,subQ0]});Q23=makeQuery(id+"F0.imprint","IMPRINT",FACE,{"disambiguationData":[TD([[makeQuery(id+"F0.imprint","IMPRINT",EDGE,{"disambiguationData":[TD([[subQ2,-1.0]])],"derivedFrom":subQ1}),1.0]])]});}
            var Q24;
            Q24=makeQuery(id+"F0.imprint","IMPRINT",FACE,{"disambiguationData":[TD([[makeQuery(id+"F0.imprint","IMPRINT",EDGE,{"derivedFrom":sQuery(id+"F0.wireOp",EDGE,"E19")}),1.0]])]});
            var Q25;
            {var subQ2=sQuery(id+"F0.wireOp",EDGE,"E19");Q25=makeQuery(id+"F0.imprint","IMPRINT",FACE,{"disambiguationData":[TD([[makeQuery(id+"F0.imprint","IMPRINT",EDGE,{"derivedFrom":subQ2}),-1.0]])]});}
            var Q26;
            {var subQ0=sQuery(id+"F0.wireOp",EDGE,"E37");var subQ1=sQuery(id+"F0.wireOp",EDGE,"E5");var subQ2=makeQuery(id+"F0.imprint","INTERSECT",VERTEX,{"derivedFrom":[subQ1,subQ0]});Q26=makeQuery(id+"F0.imprint","IMPRINT",FACE,{"disambiguationData":[TD([[makeQuery(id+"F0.imprint","IMPRINT",EDGE,{"disambiguationData":[TD([[subQ2,-1.0]])],"derivedFrom":subQ1}),1.0]])]});}
            var Q27;
            {var subQ0=sQuery(id+"F0.wireOp",EDGE,"E68");Q27=makeQuery(id+"F0.imprint","IMPRINT",FACE,{"disambiguationData":[TD([[makeQuery(id+"F0.imprint","IMPRINT",EDGE,{"derivedFrom":subQ0}),1.0]])]});}
            var Q28;
            {var subQ0=sQuery(id+"F0.wireOp",EDGE,"E39");var subQ1=sQuery(id+"F0.wireOp",EDGE,"E5");var subQ2=makeQuery(id+"F0.imprint","INTERSECT",VERTEX,{"derivedFrom":[subQ1,subQ0]});Q28=makeQuery(id+"F0.imprint","IMPRINT",FACE,{"disambiguationData":[TD([[makeQuery(id+"F0.imprint","IMPRINT",EDGE,{"disambiguationData":[TD([[subQ2,-1.0]])],"derivedFrom":subQ1}),1.0]])]});}
            var Q29;
            {var subQ2=sQuery(id+"F0.wireOp",EDGE,"E14");Q29=makeQuery(id+"F0.imprint","IMPRINT",FACE,{"disambiguationData":[TD([[makeQuery(id+"F0.imprint","IMPRINT",EDGE,{"derivedFrom":subQ2}),-1.0]])]});}
            var Q30;
            {var subQ0=sQuery(id+"F0.wireOp",EDGE,"E70");Q30=makeQuery(id+"F0.imprint","IMPRINT",FACE,{"disambiguationData":[TD([[makeQuery(id+"F0.imprint","IMPRINT",EDGE,{"derivedFrom":subQ0}),1.0]])]});}
            var Q31;
            {var subQ0=sQuery(id+"F0.wireOp",EDGE,"E41");var subQ1=sQuery(id+"F0.wireOp",EDGE,"E5");var subQ2=makeQuery(id+"F0.imprint","INTERSECT",VERTEX,{"derivedFrom":[subQ1,subQ0]});Q31=makeQuery(id+"F0.imprint","IMPRINT",FACE,{"disambiguationData":[TD([[makeQuery(id+"F0.imprint","IMPRINT",EDGE,{"disambiguationData":[TD([[subQ2,-1.0]])],"derivedFrom":subQ1}),1.0]])]});}
            var Q32;
            {var subQ2=sQuery(id+"F0.wireOp",EDGE,"E21");Q32=makeQuery(id+"F0.imprint","IMPRINT",FACE,{"disambiguationData":[TD([[makeQuery(id+"F0.imprint","IMPRINT",EDGE,{"derivedFrom":subQ2}),-1.0]])]});}
            var Q33;
            Q33=makeQuery(id+"F0.imprint","IMPRINT",FACE,{"disambiguationData":[TD([[makeQuery(id+"F0.imprint","IMPRINT",EDGE,{"derivedFrom":sQuery(id+"F0.wireOp",EDGE,"E21")}),1.0]])]});
            var Q34;
            {var subQ0=sQuery(id+"F0.wireOp",EDGE,"E43");var subQ1=sQuery(id+"F0.wireOp",EDGE,"E5");var subQ2=makeQuery(id+"F0.imprint","INTERSECT",VERTEX,{"derivedFrom":[subQ1,subQ0]});Q34=makeQuery(id+"F0.imprint","IMPRINT",FACE,{"disambiguationData":[TD([[makeQuery(id+"F0.imprint","IMPRINT",EDGE,{"disambiguationData":[TD([[subQ2,-1.0]])],"derivedFrom":subQ1}),1.0]])]});}
            var Q35;
            {var subQ1=sQuery(id+"F0.wireOp",EDGE,"E15");Q35=makeQuery(id+"F0.imprint","IMPRINT",FACE,{"disambiguationData":[TD([[makeQuery(id+"F0.imprint","IMPRINT",EDGE,{"derivedFrom":subQ1}),-1.0]])]});}
            var Q36;
            Q36=makeQuery(id+"F0.imprint","IMPRINT",FACE,{"disambiguationData":[TD([[makeQuery(id+"F0.imprint","IMPRINT",EDGE,{"derivedFrom":sQuery(id+"F0.wireOp",EDGE,"E20")}),1.0]])]});
            var Q37;
            {var subQ1=sQuery(id+"F0.wireOp",EDGE,"E20");Q37=makeQuery(id+"F0.imprint","IMPRINT",FACE,{"disambiguationData":[TD([[makeQuery(id+"F0.imprint","IMPRINT",EDGE,{"derivedFrom":subQ1}),-1.0]])]});}
            var Q38;
            {var subQ0=sQuery(id+"F0.wireOp",EDGE,"E45");var subQ1=sQuery(id+"F0.wireOp",EDGE,"E5");var subQ2=makeQuery(id+"F0.imprint","INTERSECT",VERTEX,{"derivedFrom":[subQ1,subQ0]});Q38=makeQuery(id+"F0.imprint","IMPRINT",FACE,{"disambiguationData":[TD([[makeQuery(id+"F0.imprint","IMPRINT",EDGE,{"disambiguationData":[TD([[subQ2,-1.0]])],"derivedFrom":subQ1}),1.0]])]});}
            var Q39;
            {var subQ0=sQuery(id+"F0.wireOp",EDGE,"E72");Q39=makeQuery(id+"F0.imprint","IMPRINT",FACE,{"disambiguationData":[TD([[makeQuery(id+"F0.imprint","IMPRINT",EDGE,{"derivedFrom":subQ0}),1.0]])]});}
            extrude(context, id + "F8", {"entities" : qUnion([Q0, Q1, Q2, Q3, Q4, Q5, Q6, Q7, Q8, Q9, Q10, Q11, Q12, Q13, Q14, Q15, Q16, Q17, Q18, Q19, Q20, Q21, Q22, Q23, Q24, Q25, Q26, Q27, Q28, Q29, Q30, Q31, Q32, Q33, Q34, Q35, Q36, Q37, Q38, Q39]), "oppositeDirection" : true, "depth" : 3.17 * mm, "offsetDistance" : 25.4 * mm});
        }
        {
            var Q0;
            Q0=makeQuery(id+"F2.opExtrude","SWEPT_EDGE",EDGE,{"disambiguationData":[OSD([sQuery(id+"F0.wireOp",EDGE,"E61"),sQuery(id+"F0.wireOp",EDGE,"E63")])]});
            var Q1;
            Q1=makeQuery(id+"F2.opExtrude","SWEPT_EDGE",EDGE,{"disambiguationData":[OSD([sQuery(id+"F0.wireOp",EDGE,"E47"),sQuery(id+"F0.wireOp",EDGE,"E49")])]});
            var Q2;
            Q2=makeQuery(id+"F2.opExtrude","SWEPT_EDGE",EDGE,{"disambiguationData":[OSD([sQuery(id+"F0.wireOp",EDGE,"E61"),sQuery(id+"F0.wireOp",EDGE,"E62")])]});
            var Q3;
            Q3=makeQuery(id+"F2.opExtrude","SWEPT_EDGE",EDGE,{"disambiguationData":[OSD([sQuery(id+"F0.wireOp",EDGE,"E47"),sQuery(id+"F0.wireOp",EDGE,"E48")])]});
            fillet(context, id + "F9", {"entities" : qUnion([Q0, Q1, Q2, Q3]), "radius" : 3.17 * mm, "tangentPropagation" : true, "allowEdgeOverflow" : false});
        }
        {
            var Q0;
            Q0=makeQuery(id+"F2.opExtrude","SWEPT_EDGE",EDGE,{"disambiguationData":[OSD([sQuery(id+"F0.wireOp",EDGE,"E47"),sQuery(id+"F0.wireOp",EDGE,"E50")])]});
            var Q1;
            Q1=makeQuery(id+"F2.opExtrude","SWEPT_EDGE",EDGE,{"disambiguationData":[OSD([sQuery(id+"F0.wireOp",EDGE,"E47"),sQuery(id+"F0.wireOp",EDGE,"E51")])]});
            var Q2;
            Q2=makeQuery(id+"F2.opExtrude","SWEPT_EDGE",EDGE,{"disambiguationData":[OSD([sQuery(id+"F0.wireOp",EDGE,"E61"),sQuery(id+"F0.wireOp",EDGE,"E65")])]});
            var Q3;
            Q3=makeQuery(id+"F2.opExtrude","SWEPT_EDGE",EDGE,{"disambiguationData":[OSD([sQuery(id+"F0.wireOp",EDGE,"E61"),sQuery(id+"F0.wireOp",EDGE,"E64")])]});
            fillet(context, id + "F10", {"entities" : qUnion([Q0, Q1, Q2, Q3]), "radius" : 3.17 * mm, "tangentPropagation" : true, "allowEdgeOverflow" : false});
        }
        {
            var Q0;
            Q0=makeQuery(id+"F2.opExtrude","SWEPT_EDGE",EDGE,{"disambiguationData":[OSD([sQuery(id+"F0.wireOp",EDGE,"E61"),sQuery(id+"F0.wireOp",EDGE,"E66")])]});
            var Q1;
            Q1=makeQuery(id+"F2.opExtrude","SWEPT_EDGE",EDGE,{"disambiguationData":[OSD([sQuery(id+"F0.wireOp",EDGE,"E61"),sQuery(id+"F0.wireOp",EDGE,"E67")])]});
            var Q2;
            Q2=makeQuery(id+"F2.opExtrude","SWEPT_EDGE",EDGE,{"disambiguationData":[OSD([sQuery(id+"F0.wireOp",EDGE,"E47"),sQuery(id+"F0.wireOp",EDGE,"E52")])]});
            var Q3;
            Q3=makeQuery(id+"F2.opExtrude","SWEPT_EDGE",EDGE,{"disambiguationData":[OSD([sQuery(id+"F0.wireOp",EDGE,"E47"),sQuery(id+"F0.wireOp",EDGE,"E53")])]});
            var Q4;
            Q4=makeQuery(id+"F2.opExtrude","SWEPT_EDGE",EDGE,{"disambiguationData":[OSD([sQuery(id+"F0.wireOp",EDGE,"E47"),sQuery(id+"F0.wireOp",EDGE,"E54")])]});
            var Q5;
            Q5=makeQuery(id+"F2.opExtrude","SWEPT_EDGE",EDGE,{"disambiguationData":[OSD([sQuery(id+"F0.wireOp",EDGE,"E61"),sQuery(id+"F0.wireOp",EDGE,"E68")])]});
            var Q6;
            Q6=makeQuery(id+"F2.opExtrude","SWEPT_EDGE",EDGE,{"disambiguationData":[OSD([sQuery(id+"F0.wireOp",EDGE,"E61"),sQuery(id+"F0.wireOp",EDGE,"E69")])]});
            var Q7;
            Q7=makeQuery(id+"F2.opExtrude","SWEPT_EDGE",EDGE,{"disambiguationData":[OSD([sQuery(id+"F0.wireOp",EDGE,"E47"),sQuery(id+"F0.wireOp",EDGE,"E55")])]});
            fillet(context, id + "F11", {"entities" : qUnion([Q0, Q1, Q2, Q3, Q4, Q5, Q6, Q7]), "radius" : 3.17 * mm, "tangentPropagation" : true, "allowEdgeOverflow" : false});
        }
        {
            var Q0;
            Q0=makeQuery(id+"F2.opExtrude","SWEPT_EDGE",EDGE,{"disambiguationData":[OSD([sQuery(id+"F0.wireOp",EDGE,"E47"),sQuery(id+"F0.wireOp",EDGE,"E57")])]});
            var Q1;
            Q1=makeQuery(id+"F2.opExtrude","SWEPT_EDGE",EDGE,{"disambiguationData":[OSD([sQuery(id+"F0.wireOp",EDGE,"E61"),sQuery(id+"F0.wireOp",EDGE,"E71")])]});
            var Q2;
            Q2=makeQuery(id+"F2.opExtrude","SWEPT_EDGE",EDGE,{"disambiguationData":[OSD([sQuery(id+"F0.wireOp",EDGE,"E61"),sQuery(id+"F0.wireOp",EDGE,"E70")])]});
            var Q3;
            Q3=makeQuery(id+"F2.opExtrude","SWEPT_EDGE",EDGE,{"disambiguationData":[OSD([sQuery(id+"F0.wireOp",EDGE,"E47"),sQuery(id+"F0.wireOp",EDGE,"E56")])]});
            var Q4;
            Q4=makeQuery(id+"F2.opExtrude","SWEPT_EDGE",EDGE,{"disambiguationData":[OSD([sQuery(id+"F0.wireOp",EDGE,"E47"),sQuery(id+"F0.wireOp",EDGE,"E58")])]});
            var Q5;
            Q5=makeQuery(id+"F2.opExtrude","SWEPT_EDGE",EDGE,{"disambiguationData":[OSD([sQuery(id+"F0.wireOp",EDGE,"E61"),sQuery(id+"F0.wireOp",EDGE,"E72")])]});
            var Q6;
            Q6=makeQuery(id+"F2.opExtrude","SWEPT_EDGE",EDGE,{"disambiguationData":[OSD([sQuery(id+"F0.wireOp",EDGE,"E61"),sQuery(id+"F0.wireOp",EDGE,"E73")])]});
            var Q7;
            Q7=makeQuery(id+"F2.opExtrude","SWEPT_EDGE",EDGE,{"disambiguationData":[OSD([sQuery(id+"F0.wireOp",EDGE,"E47"),sQuery(id+"F0.wireOp",EDGE,"E59")])]});
            fillet(context, id + "F12", {"entities" : qUnion([Q0, Q1, Q2, Q3, Q4, Q5, Q6, Q7]), "radius" : 3.17 * mm, "tangentPropagation" : true, "allowEdgeOverflow" : false});
        }
        {
            var Q0;
            Q0=makeQuery(id+"F1.opExtrude","SWEPT_EDGE",EDGE,{"disambiguationData":[OSD([sQuery(id+"F0.wireOp",EDGE,"E0.bottom"),sQuery(id+"F0.wireOp",EDGE,"E0.left")])]});
            var Q1;
            Q1=makeQuery(id+"F7.opExtrude","SWEPT_EDGE",EDGE,{"disambiguationData":[OSD([sQuery(id+"F0.wireOp",EDGE,"E0.bottom"),sQuery(id+"F0.wireOp",EDGE,"E0.left")])]});
            var Q2;
            Q2=makeQuery(id+"F4.opExtrude","SWEPT_EDGE",EDGE,{"disambiguationData":[OSD([sQuery(id+"F0.wireOp",EDGE,"E0.top"),sQuery(id+"F0.wireOp",EDGE,"E0.left")])]});
            var Q3;
            Q3=makeQuery(id+"F7.opExtrude","SWEPT_EDGE",EDGE,{"disambiguationData":[OSD([sQuery(id+"F0.wireOp",EDGE,"E0.top"),sQuery(id+"F0.wireOp",EDGE,"E0.left")])]});
            var Q4;
            Q4=makeQuery(id+"F4.opExtrude","SWEPT_EDGE",EDGE,{"disambiguationData":[OSD([sQuery(id+"F0.wireOp",EDGE,"E0.top"),sQuery(id+"F0.wireOp",EDGE,"E0.right")])]});
            var Q5;
            Q5=makeQuery(id+"F7.opExtrude","SWEPT_EDGE",EDGE,{"disambiguationData":[OSD([sQuery(id+"F0.wireOp",EDGE,"E0.top"),sQuery(id+"F0.wireOp",EDGE,"E0.right")])]});
            var Q6;
            Q6=makeQuery(id+"F3.opExtrude","SWEPT_EDGE",EDGE,{"disambiguationData":[OSD([sQuery(id+"F0.wireOp",EDGE,"E0.bottom"),sQuery(id+"F0.wireOp",EDGE,"E0.right")])]});
            var Q7;
            Q7=makeQuery(id+"F7.opExtrude","SWEPT_EDGE",EDGE,{"disambiguationData":[OSD([sQuery(id+"F0.wireOp",EDGE,"E0.bottom"),sQuery(id+"F0.wireOp",EDGE,"E0.right")])]});
            fillet(context, id + "F13", {"entities" : qUnion([Q0, Q1, Q2, Q3, Q4, Q5, Q6, Q7]), "radius" : 3.17 * mm, "tangentPropagation" : true, "allowEdgeOverflow" : false});
        }
    });
